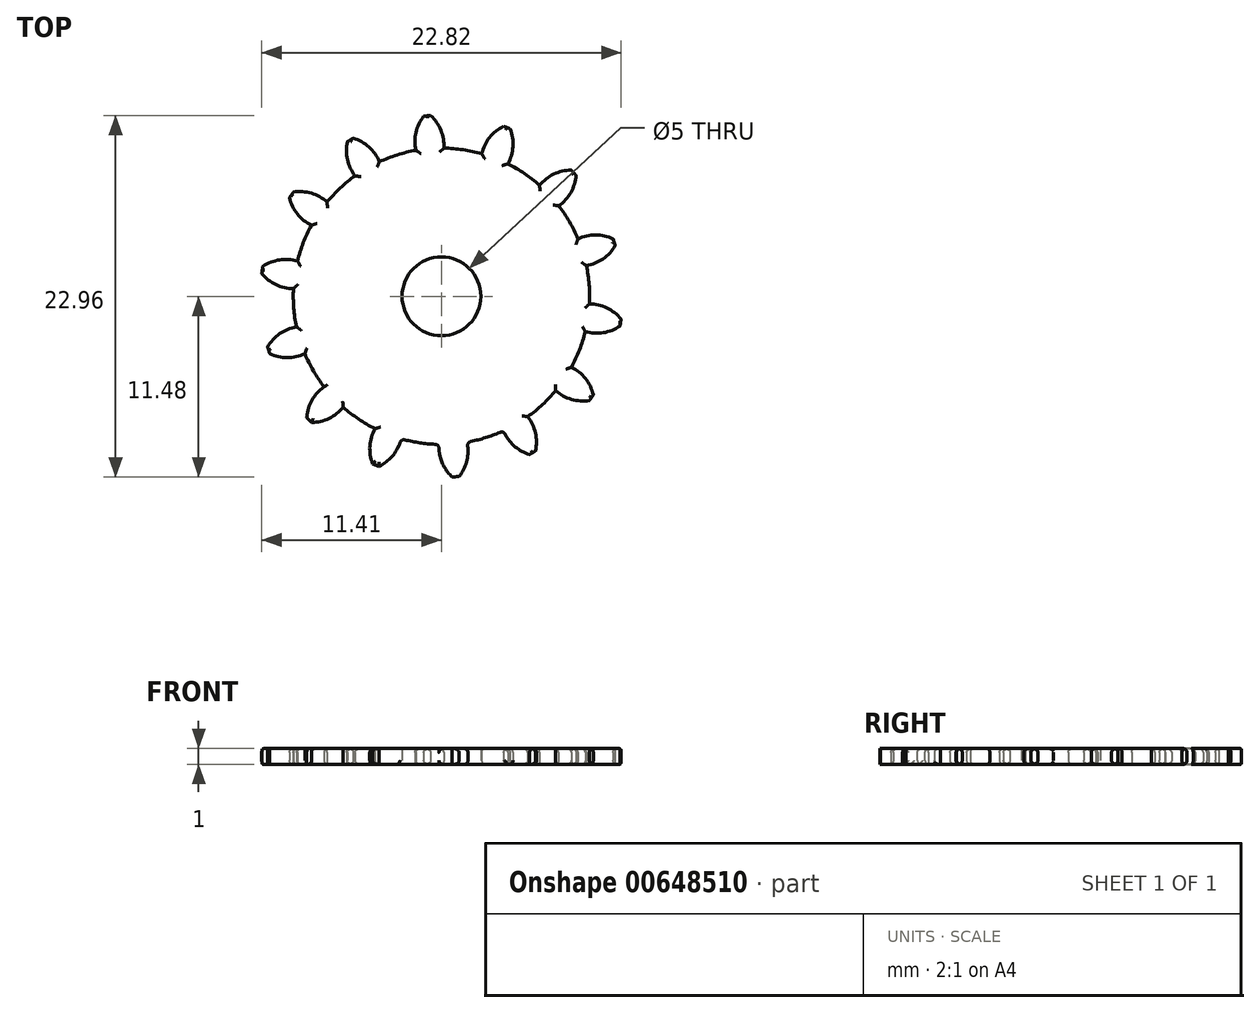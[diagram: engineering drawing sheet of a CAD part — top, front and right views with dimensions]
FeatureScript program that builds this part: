
annotation { "Feature Type Name" : "Feature", "Feature Type Description" : "" }
export const myFeature = defineFeature(function(context is Context, id is Id, definition is map)
    precondition{}
    {
        {
            assignVariable(context, id + "F0", {"name" : "GearDepth", "anyValue" : 1});
        }
        {
            assignVariable(context, id + "F1", {"name" : "TeethFillet", "anyValue" : getVariable(context, 'GearDepth') * .25});
        }
        {
            var Q0;
            Q0=qCreatedBy(makeId("Top.planeOp"),FACE);
            var sketch = newSketch(context, id + "F2", { "sketchPlane" : qUnion([Q0])});
            skCircle(sketch, "E0", {"center": v(0, 0) * mm, "radius": 9.4 * mm});
            skCircle(sketch, "E1", {"center": v(0, 0) * mm, "radius": 10.45 * mm, "construction": true});
            skCircle(sketch, "E2", {"center": v(0, 0) * mm, "radius": 11.5 * mm, "construction": true});
            skLineSegment(sketch, "E3", {"start": v(0, 0) * mm, "end": v(0, 17.6) * mm, "construction": true});
            skLineSegment(sketch, "E4", {"start": v(0, 0) * mm, "end": v(-1.42, 18) * mm, "construction": true});
            skLineSegment(sketch, "E5", {"start": v(0, 10.45) * mm, "end": v(-10.54, 10.45) * mm, "construction": true});
            skLineSegment(sketch, "E6", {"start": v(0, 10.45) * mm, "end": v(-10.3, 6.7) * mm, "construction": true});
            skCircle(sketch, "E7", {"center": v(0, 10.45) * mm, "radius": 2.61 * mm, "construction": true});
            skCircle(sketch, "E8", {"center": v(-2.46, 9.56) * mm, "radius": 2.61 * mm, "construction": true});
            skArc(sketch, "E9", {"start": v(-4.91, 10.45) * mm, "mid": v(-4.92, 10.42) * mm, "end": v(-4.94, 10.39) * mm});
            skArc(sketch, "E10.trimOffspring", {"start": v(0.15, 9.4) * mm, "mid": v(-0.03, 10.54) * mm, "end": v(-0.68, 11.48) * mm});
            skArc(sketch, "E11.MirrorCS", {"start": v(-1.62, 9.27) * mm, "mid": v(-1.62, 10.41) * mm, "end": v(-1.12, 11.45) * mm});
            skLineSegment(sketch, "E12", {"start": v(-1.12, 11.45) * mm, "end": v(-0.68, 11.48) * mm});
            skArc(sketch, "E13.1.0", {"start": v(-3.94, 8.54) * mm, "mid": v(-4.6, 9.48) * mm, "end": v(-5.6, 10.05) * mm});
            skLineSegment(sketch, "E13.1.1", {"start": v(-5.98, 9.82) * mm, "end": v(-5.6, 10.05) * mm});
            skArc(sketch, "E13.1.2", {"start": v(-5.48, 7.65) * mm, "mid": v(-5.97, 8.68) * mm, "end": v(-5.98, 9.82) * mm});
            skArc(sketch, "E13.2.0", {"start": v(-7.26, 5.99) * mm, "mid": v(-8.26, 6.55) * mm, "end": v(-9.4, 6.62) * mm});
            skLineSegment(sketch, "E13.2.1", {"start": v(-9.65, 6.26) * mm, "end": v(-9.4, 6.62) * mm});
            skArc(sketch, "E13.2.2", {"start": v(-8.26, 4.5) * mm, "mid": v(-9.15, 5.23) * mm, "end": v(-9.65, 6.26) * mm});
            skArc(sketch, "E13.3.0", {"start": v(-9.14, 2.24) * mm, "mid": v(-10.28, 2.31) * mm, "end": v(-11.34, 1.89) * mm});
            skLineSegment(sketch, "E13.3.1", {"start": v(-11.4, 1.45) * mm, "end": v(-11.34, 1.89) * mm});
            skArc(sketch, "E13.3.2", {"start": v(-9.4, 0.48) * mm, "mid": v(-10.51, 0.74) * mm, "end": v(-11.4, 1.45) * mm});
            skArc(sketch, "E13.4.0", {"start": v(-9.2, -1.94) * mm, "mid": v(-10.27, -2.38) * mm, "end": v(-11.04, -3.22) * mm});
            skLineSegment(sketch, "E13.4.1", {"start": v(-10.9, -3.64) * mm, "end": v(-11.04, -3.22) * mm});
            skArc(sketch, "E13.4.2", {"start": v(-8.67, -3.64) * mm, "mid": v(-9.8, -3.9) * mm, "end": v(-10.9, -3.64) * mm});
            skArc(sketch, "E13.5.0", {"start": v(-7.45, -5.75) * mm, "mid": v(-8.22, -6.6) * mm, "end": v(-8.55, -7.7) * mm});
            skLineSegment(sketch, "E13.5.1", {"start": v(-8.25, -8.01) * mm, "end": v(-8.55, -7.7) * mm});
            skArc(sketch, "E13.5.2", {"start": v(-6.23, -7.05) * mm, "mid": v(-7.13, -7.76) * mm, "end": v(-8.25, -8.01) * mm});
            skArc(sketch, "E13.6.0", {"start": v(-4.22, -8.4) * mm, "mid": v(-4.54, -9.5) * mm, "end": v(-4.37, -10.64) * mm});
            skLineSegment(sketch, "E13.6.1", {"start": v(-3.95, -10.8) * mm, "end": v(-4.37, -10.64) * mm});
            skArc(sketch, "E13.6.2", {"start": v(-2.56, -9.05) * mm, "mid": v(-3.06, -10.08) * mm, "end": v(-3.95, -10.8) * mm});
            skArc(sketch, "E13.7.0", {"start": v(-0.15, -9.4) * mm, "mid": v(0.03, -10.54) * mm, "end": v(0.68, -11.48) * mm});
            skLineSegment(sketch, "E13.7.1", {"start": v(1.12, -11.45) * mm, "end": v(0.68, -11.48) * mm});
            skArc(sketch, "E13.7.2", {"start": v(1.62, -9.27) * mm, "mid": v(1.62, -10.41) * mm, "end": v(1.12, -11.45) * mm});
            skArc(sketch, "E13.8.0", {"start": v(3.94, -8.54) * mm, "mid": v(4.6, -9.48) * mm, "end": v(5.6, -10.05) * mm});
            skLineSegment(sketch, "E13.8.1", {"start": v(5.98, -9.82) * mm, "end": v(5.6, -10.05) * mm});
            skArc(sketch, "E13.8.2", {"start": v(5.48, -7.65) * mm, "mid": v(5.97, -8.68) * mm, "end": v(5.98, -9.82) * mm});
            skArc(sketch, "E13.9.0", {"start": v(7.26, -5.99) * mm, "mid": v(8.26, -6.55) * mm, "end": v(9.4, -6.62) * mm});
            skLineSegment(sketch, "E13.9.1", {"start": v(9.65, -6.26) * mm, "end": v(9.4, -6.62) * mm});
            skArc(sketch, "E13.9.2", {"start": v(8.26, -4.5) * mm, "mid": v(9.15, -5.23) * mm, "end": v(9.65, -6.26) * mm});
            skArc(sketch, "E13.10.0", {"start": v(9.14, -2.24) * mm, "mid": v(10.28, -2.31) * mm, "end": v(11.34, -1.89) * mm});
            skLineSegment(sketch, "E13.10.1", {"start": v(11.4, -1.45) * mm, "end": v(11.34, -1.89) * mm});
            skArc(sketch, "E13.10.2", {"start": v(9.4, -0.48) * mm, "mid": v(10.51, -0.74) * mm, "end": v(11.4, -1.45) * mm});
            skArc(sketch, "E13.11.0", {"start": v(9.2, 1.94) * mm, "mid": v(10.27, 2.38) * mm, "end": v(11.04, 3.22) * mm});
            skLineSegment(sketch, "E13.11.1", {"start": v(10.9, 3.64) * mm, "end": v(11.04, 3.22) * mm});
            skArc(sketch, "E13.11.2", {"start": v(8.67, 3.64) * mm, "mid": v(9.8, 3.9) * mm, "end": v(10.9, 3.64) * mm});
            skArc(sketch, "E13.12.0", {"start": v(7.45, 5.75) * mm, "mid": v(8.22, 6.6) * mm, "end": v(8.55, 7.7) * mm});
            skLineSegment(sketch, "E13.12.1", {"start": v(8.25, 8.01) * mm, "end": v(8.55, 7.7) * mm});
            skArc(sketch, "E13.12.2", {"start": v(6.23, 7.05) * mm, "mid": v(7.13, 7.76) * mm, "end": v(8.25, 8.01) * mm});
            skArc(sketch, "E13.13.0", {"start": v(4.22, 8.4) * mm, "mid": v(4.54, 9.5) * mm, "end": v(4.37, 10.64) * mm});
            skLineSegment(sketch, "E13.13.1", {"start": v(3.95, 10.8) * mm, "end": v(4.37, 10.64) * mm});
            skArc(sketch, "E13.13.2", {"start": v(2.56, 9.05) * mm, "mid": v(3.06, 10.08) * mm, "end": v(3.95, 10.8) * mm});
            skCircle(sketch, "E14", {"center": v(0, 0) * mm, "radius": 2.5 * mm});
            skSolve(sketch);
        }
        {
            var Q0;
            {var subQ0=sQuery(id+"F2.wireOp",EDGE,"E10.trimOffspring");Q0=makeQuery(id+"F2.imprint","IMPRINT",FACE,{"disambiguationData":[TD([[makeQuery(id+"F2.imprint","IMPRINT",EDGE,{"derivedFrom":subQ0}),1.0]])]});}
            var Q1;
            {var subQ0=sQuery(id+"F2.wireOp",EDGE,"E0");var subQ1=makeQuery(id+"F2.imprint","INTERSECT",VERTEX,{"derivedFrom":[subQ0,sQuery(id+"F2.wireOp",EDGE,"E10.trimOffspring")]});Q1=makeQuery(id+"F2.imprint","IMPRINT",FACE,{"disambiguationData":[TD([[makeQuery(id+"F2.imprint","IMPRINT",EDGE,{"disambiguationData":[TD([[subQ1,-1.0]])],"derivedFrom":subQ0}),1.0]])]});}
            var Q2;
            {var subQ0=sQuery(id+"F2.wireOp",EDGE,"E13.1.0");Q2=makeQuery(id+"F2.imprint","IMPRINT",FACE,{"disambiguationData":[TD([[makeQuery(id+"F2.imprint","IMPRINT",EDGE,{"derivedFrom":subQ0}),1.0]])]});}
            var Q3;
            {var subQ0=sQuery(id+"F2.wireOp",EDGE,"E13.2.0");Q3=makeQuery(id+"F2.imprint","IMPRINT",FACE,{"disambiguationData":[TD([[makeQuery(id+"F2.imprint","IMPRINT",EDGE,{"derivedFrom":subQ0}),1.0]])]});}
            var Q4;
            {var subQ0=sQuery(id+"F2.wireOp",EDGE,"E13.3.0");Q4=makeQuery(id+"F2.imprint","IMPRINT",FACE,{"disambiguationData":[TD([[makeQuery(id+"F2.imprint","IMPRINT",EDGE,{"derivedFrom":subQ0}),1.0]])]});}
            var Q5;
            {var subQ0=sQuery(id+"F2.wireOp",EDGE,"E13.4.0");Q5=makeQuery(id+"F2.imprint","IMPRINT",FACE,{"disambiguationData":[TD([[makeQuery(id+"F2.imprint","IMPRINT",EDGE,{"derivedFrom":subQ0}),1.0]])]});}
            var Q6;
            {var subQ0=sQuery(id+"F2.wireOp",EDGE,"E13.5.0");Q6=makeQuery(id+"F2.imprint","IMPRINT",FACE,{"disambiguationData":[TD([[makeQuery(id+"F2.imprint","IMPRINT",EDGE,{"derivedFrom":subQ0}),1.0]])]});}
            var Q7;
            {var subQ0=sQuery(id+"F2.wireOp",EDGE,"E13.6.0");Q7=makeQuery(id+"F2.imprint","IMPRINT",FACE,{"disambiguationData":[TD([[makeQuery(id+"F2.imprint","IMPRINT",EDGE,{"derivedFrom":subQ0}),1.0]])]});}
            var Q8;
            {var subQ0=sQuery(id+"F2.wireOp",EDGE,"E13.7.0");Q8=makeQuery(id+"F2.imprint","IMPRINT",FACE,{"disambiguationData":[TD([[makeQuery(id+"F2.imprint","IMPRINT",EDGE,{"derivedFrom":subQ0}),1.0]])]});}
            var Q9;
            {var subQ0=sQuery(id+"F2.wireOp",EDGE,"E13.8.0");Q9=makeQuery(id+"F2.imprint","IMPRINT",FACE,{"disambiguationData":[TD([[makeQuery(id+"F2.imprint","IMPRINT",EDGE,{"derivedFrom":subQ0}),1.0]])]});}
            var Q10;
            {var subQ0=sQuery(id+"F2.wireOp",EDGE,"E13.9.0");Q10=makeQuery(id+"F2.imprint","IMPRINT",FACE,{"disambiguationData":[TD([[makeQuery(id+"F2.imprint","IMPRINT",EDGE,{"derivedFrom":subQ0}),1.0]])]});}
            var Q11;
            {var subQ0=sQuery(id+"F2.wireOp",EDGE,"E13.10.0");Q11=makeQuery(id+"F2.imprint","IMPRINT",FACE,{"disambiguationData":[TD([[makeQuery(id+"F2.imprint","IMPRINT",EDGE,{"derivedFrom":subQ0}),1.0]])]});}
            var Q12;
            {var subQ0=sQuery(id+"F2.wireOp",EDGE,"E13.11.0");Q12=makeQuery(id+"F2.imprint","IMPRINT",FACE,{"disambiguationData":[TD([[makeQuery(id+"F2.imprint","IMPRINT",EDGE,{"derivedFrom":subQ0}),1.0]])]});}
            var Q13;
            {var subQ0=sQuery(id+"F2.wireOp",EDGE,"E13.12.0");Q13=makeQuery(id+"F2.imprint","IMPRINT",FACE,{"disambiguationData":[TD([[makeQuery(id+"F2.imprint","IMPRINT",EDGE,{"derivedFrom":subQ0}),1.0]])]});}
            var Q14;
            {var subQ0=sQuery(id+"F2.wireOp",EDGE,"E13.13.0");Q14=makeQuery(id+"F2.imprint","IMPRINT",FACE,{"disambiguationData":[TD([[makeQuery(id+"F2.imprint","IMPRINT",EDGE,{"derivedFrom":subQ0}),1.0]])]});}
            var Q15;
            {var subQ0=sQuery(id+"F2.wireOp",EDGE,"E13.14.0");Q15=makeQuery(id+"F2.imprint","IMPRINT",FACE,{"disambiguationData":[TD([[makeQuery(id+"F2.imprint","IMPRINT",EDGE,{"derivedFrom":subQ0}),1.0]])]});}
            var Q16;
            {var subQ0=sQuery(id+"F2.wireOp",EDGE,"E13.15.0");Q16=makeQuery(id+"F2.imprint","IMPRINT",FACE,{"disambiguationData":[TD([[makeQuery(id+"F2.imprint","IMPRINT",EDGE,{"derivedFrom":subQ0}),1.0]])]});}
            var Q17;
            {var subQ0=sQuery(id+"F2.wireOp",EDGE,"E13.16.0");Q17=makeQuery(id+"F2.imprint","IMPRINT",FACE,{"disambiguationData":[TD([[makeQuery(id+"F2.imprint","IMPRINT",EDGE,{"derivedFrom":subQ0}),1.0]])]});}
            var Q18;
            {var subQ0=sQuery(id+"F2.wireOp",EDGE,"E13.17.0");Q18=makeQuery(id+"F2.imprint","IMPRINT",FACE,{"disambiguationData":[TD([[makeQuery(id+"F2.imprint","IMPRINT",EDGE,{"derivedFrom":subQ0}),1.0]])]});}
            var Q19;
            {var subQ0=sQuery(id+"F2.wireOp",EDGE,"E13.18.0");Q19=makeQuery(id+"F2.imprint","IMPRINT",FACE,{"disambiguationData":[TD([[makeQuery(id+"F2.imprint","IMPRINT",EDGE,{"derivedFrom":subQ0}),1.0]])]});}
            var Q20;
            {var subQ0=sQuery(id+"F2.wireOp",EDGE,"E13.19.0");Q20=makeQuery(id+"F2.imprint","IMPRINT",FACE,{"disambiguationData":[TD([[makeQuery(id+"F2.imprint","IMPRINT",EDGE,{"derivedFrom":subQ0}),1.0]])]});}
            var Q21;
            Q21=sQuery(id+"F2.wireOp",EDGE,"E0");
            var Q22;
            Q22=sQuery(id+"F2.wireOp",EDGE,"E10.trimOffspring");
            var Q23;
            Q23=sQuery(id+"F2.wireOp",EDGE,"E12");
            var Q24;
            Q24=sQuery(id+"F2.wireOp",EDGE,"E11.MirrorCS");
            extrude(context, id + "F3", {"entities" : qUnion([Q0, Q1, Q2, Q3, Q4, Q5, Q6, Q7, Q8, Q9, Q10, Q11, Q12, Q13, Q14, Q15, Q16, Q17, Q18, Q19, Q20]), "surfaceEntities" : qUnion([Q21, Q22, Q23, Q24]), "depth" : (getVariable(context, 'GearDepth')) * mm});
        }
        {
            var Q0;
            Q0=makeQuery(id+"F3.opExtrude","CAP_EDGE",EDGE,{"disambiguationData":[OSD([sQuery(id+"F2.wireOp",EDGE,"E13.5.2")])],"isStart":false});
            var Q1;
            Q1=makeQuery(id+"F3.opExtrude","CAP_EDGE",EDGE,{"disambiguationData":[OSD([sQuery(id+"F2.wireOp",EDGE,"E13.5.1")])],"isStart":false});
            var Q2;
            {var subQ0=sQuery(id+"F2.wireOp",EDGE,"E0");Q2=makeQuery(id+"F3.opExtrude","CAP_EDGE",EDGE,{"disambiguationData":[OSD([subQ0]),TDD([makeQuery(id+"F2.imprint","IMPRINT",EDGE,{"disambiguationData":[TD([[makeQuery(id+"F2.imprint","INTERSECT",VERTEX,{"derivedFrom":[subQ0,sQuery(id+"F2.wireOp",EDGE,"E13.5.2")]}),-1.0]])],"derivedFrom":subQ0})])],"isStart":false});}
            var Q3;
            Q3=makeQuery(id+"F3.opExtrude","CAP_EDGE",EDGE,{"disambiguationData":[OSD([sQuery(id+"F2.wireOp",EDGE,"E13.6.0")])],"isStart":false});
            var Q4;
            Q4=makeQuery(id+"F3.opExtrude","CAP_EDGE",EDGE,{"disambiguationData":[OSD([sQuery(id+"F2.wireOp",EDGE,"E13.6.1")])],"isStart":false});
            var Q5;
            Q5=makeQuery(id+"F3.opExtrude","CAP_EDGE",EDGE,{"disambiguationData":[OSD([sQuery(id+"F2.wireOp",EDGE,"E13.6.2")])],"isStart":false});
            var Q6;
            {var subQ0=sQuery(id+"F2.wireOp",EDGE,"E0");Q6=makeQuery(id+"F3.opExtrude","SWEPT_FACE",FACE,{"disambiguationData":[OSD([subQ0]),TDD([makeQuery(id+"F2.imprint","IMPRINT",EDGE,{"disambiguationData":[TD([[makeQuery(id+"F2.imprint","INTERSECT",VERTEX,{"derivedFrom":[subQ0,sQuery(id+"F2.wireOp",EDGE,"E13.6.2")]}),-1.0]])],"derivedFrom":subQ0})])]});}
            var Q7;
            {var subQ0=sQuery(id+"F2.wireOp",EDGE,"E0");Q7=makeQuery(id+"F3.opExtrude","CAP_EDGE",EDGE,{"disambiguationData":[OSD([subQ0]),TDD([makeQuery(id+"F2.imprint","IMPRINT",EDGE,{"disambiguationData":[TD([[makeQuery(id+"F2.imprint","INTERSECT",VERTEX,{"derivedFrom":[subQ0,sQuery(id+"F2.wireOp",EDGE,"E13.6.2")]}),-1.0]])],"derivedFrom":subQ0})])],"isStart":false});}
            var Q8;
            Q8=makeQuery(id+"F3.opExtrude","CAP_EDGE",EDGE,{"disambiguationData":[OSD([sQuery(id+"F2.wireOp",EDGE,"E13.7.2")])],"isStart":true});
            var Q9;
            {var subQ0=sQuery(id+"F2.wireOp",EDGE,"E0");Q9=makeQuery(id+"F3.opExtrude","CAP_EDGE",EDGE,{"disambiguationData":[OSD([subQ0]),TDD([makeQuery(id+"F2.imprint","IMPRINT",EDGE,{"disambiguationData":[TD([[makeQuery(id+"F2.imprint","INTERSECT",VERTEX,{"derivedFrom":[subQ0,sQuery(id+"F2.wireOp",EDGE,"E13.7.2")]}),-1.0]])],"derivedFrom":subQ0})])],"isStart":true});}
            var Q10;
            Q10=makeQuery(id+"F3.opExtrude","CAP_EDGE",EDGE,{"disambiguationData":[OSD([sQuery(id+"F2.wireOp",EDGE,"E13.7.2")])],"isStart":false});
            var Q11;
            {var subQ0=sQuery(id+"F2.wireOp",EDGE,"E0");Q11=makeQuery(id+"F3.opExtrude","CAP_EDGE",EDGE,{"disambiguationData":[OSD([subQ0]),TDD([makeQuery(id+"F2.imprint","IMPRINT",EDGE,{"disambiguationData":[TD([[makeQuery(id+"F2.imprint","INTERSECT",VERTEX,{"derivedFrom":[subQ0,sQuery(id+"F2.wireOp",EDGE,"E13.7.2")]}),-1.0]])],"derivedFrom":subQ0})])],"isStart":false});}
            var Q12;
            Q12=makeQuery(id+"F3.opExtrude","CAP_EDGE",EDGE,{"disambiguationData":[OSD([sQuery(id+"F2.wireOp",EDGE,"E13.8.0")])],"isStart":false});
            var Q13;
            {var subQ0=sQuery(id+"F2.wireOp",EDGE,"E0");Q13=makeQuery(id+"F3.opExtrude","SWEPT_FACE",FACE,{"disambiguationData":[OSD([subQ0]),TDD([makeQuery(id+"F2.imprint","IMPRINT",EDGE,{"disambiguationData":[TD([[makeQuery(id+"F2.imprint","INTERSECT",VERTEX,{"derivedFrom":[subQ0,sQuery(id+"F2.wireOp",EDGE,"E13.7.2")]}),-1.0]])],"derivedFrom":subQ0})])]});}
            var Q14;
            Q14=makeQuery(id+"F3.opExtrude","CAP_EDGE",EDGE,{"disambiguationData":[OSD([sQuery(id+"F2.wireOp",EDGE,"E13.6.0")])],"isStart":true});
            var Q15;
            Q15=makeQuery(id+"F3.opExtrude","CAP_EDGE",EDGE,{"disambiguationData":[OSD([sQuery(id+"F2.wireOp",EDGE,"E13.8.2")])],"isStart":false});
            var Q16;
            {var subQ0=sQuery(id+"F2.wireOp",EDGE,"E0");Q16=makeQuery(id+"F3.opExtrude","CAP_EDGE",EDGE,{"disambiguationData":[OSD([subQ0]),TDD([makeQuery(id+"F2.imprint","IMPRINT",EDGE,{"disambiguationData":[TD([[makeQuery(id+"F2.imprint","INTERSECT",VERTEX,{"derivedFrom":[subQ0,sQuery(id+"F2.wireOp",EDGE,"E13.8.2")]}),-1.0]])],"derivedFrom":subQ0})])],"isStart":false});}
            var Q17;
            Q17=makeQuery(id+"F3.opExtrude","CAP_EDGE",EDGE,{"disambiguationData":[OSD([sQuery(id+"F2.wireOp",EDGE,"E13.9.0")])],"isStart":false});
            var Q18;
            Q18=makeQuery(id+"F3.opExtrude","CAP_EDGE",EDGE,{"disambiguationData":[OSD([sQuery(id+"F2.wireOp",EDGE,"E13.9.2")])],"isStart":false});
            var Q19;
            {var subQ0=sQuery(id+"F2.wireOp",EDGE,"E0");Q19=makeQuery(id+"F3.opExtrude","CAP_EDGE",EDGE,{"disambiguationData":[OSD([subQ0]),TDD([makeQuery(id+"F2.imprint","IMPRINT",EDGE,{"disambiguationData":[TD([[makeQuery(id+"F2.imprint","INTERSECT",VERTEX,{"derivedFrom":[subQ0,sQuery(id+"F2.wireOp",EDGE,"E13.9.2")]}),-1.0]])],"derivedFrom":subQ0})])],"isStart":false});}
            var Q20;
            Q20=makeQuery(id+"F3.opExtrude","CAP_EDGE",EDGE,{"disambiguationData":[OSD([sQuery(id+"F2.wireOp",EDGE,"E13.10.0")])],"isStart":false});
            var Q21;
            Q21=makeQuery(id+"F3.opExtrude","CAP_EDGE",EDGE,{"disambiguationData":[OSD([sQuery(id+"F2.wireOp",EDGE,"E13.10.2")])],"isStart":false});
            var Q22;
            {var subQ0=sQuery(id+"F2.wireOp",EDGE,"E0");Q22=makeQuery(id+"F3.opExtrude","CAP_EDGE",EDGE,{"disambiguationData":[OSD([subQ0]),TDD([makeQuery(id+"F2.imprint","IMPRINT",EDGE,{"disambiguationData":[TD([[makeQuery(id+"F2.imprint","INTERSECT",VERTEX,{"derivedFrom":[subQ0,sQuery(id+"F2.wireOp",EDGE,"E13.10.2")]}),-1.0]])],"derivedFrom":subQ0})])],"isStart":false});}
            var Q23;
            Q23=makeQuery(id+"F3.opExtrude","CAP_EDGE",EDGE,{"disambiguationData":[OSD([sQuery(id+"F2.wireOp",EDGE,"E13.11.0")])],"isStart":false});
            var Q24;
            Q24=makeQuery(id+"F3.opExtrude","CAP_EDGE",EDGE,{"disambiguationData":[OSD([sQuery(id+"F2.wireOp",EDGE,"E13.11.2")])],"isStart":false});
            var Q25;
            {var subQ0=sQuery(id+"F2.wireOp",EDGE,"E0");Q25=makeQuery(id+"F3.opExtrude","CAP_EDGE",EDGE,{"disambiguationData":[OSD([subQ0]),TDD([makeQuery(id+"F2.imprint","IMPRINT",EDGE,{"disambiguationData":[TD([[makeQuery(id+"F2.imprint","INTERSECT",VERTEX,{"derivedFrom":[subQ0,sQuery(id+"F2.wireOp",EDGE,"E13.11.2")]}),-1.0]])],"derivedFrom":subQ0})])],"isStart":false});}
            var Q26;
            Q26=makeQuery(id+"F3.opExtrude","CAP_EDGE",EDGE,{"disambiguationData":[OSD([sQuery(id+"F2.wireOp",EDGE,"E13.12.0")])],"isStart":false});
            var Q27;
            Q27=makeQuery(id+"F3.opExtrude","CAP_EDGE",EDGE,{"disambiguationData":[OSD([sQuery(id+"F2.wireOp",EDGE,"E13.12.2")])],"isStart":false});
            var Q28;
            {var subQ0=sQuery(id+"F2.wireOp",EDGE,"E0");Q28=makeQuery(id+"F3.opExtrude","CAP_EDGE",EDGE,{"disambiguationData":[OSD([subQ0]),TDD([makeQuery(id+"F2.imprint","IMPRINT",EDGE,{"disambiguationData":[TD([[makeQuery(id+"F2.imprint","INTERSECT",VERTEX,{"derivedFrom":[subQ0,sQuery(id+"F2.wireOp",EDGE,"E13.12.2")]}),-1.0]])],"derivedFrom":subQ0})])],"isStart":false});}
            var Q29;
            Q29=makeQuery(id+"F3.opExtrude","CAP_EDGE",EDGE,{"disambiguationData":[OSD([sQuery(id+"F2.wireOp",EDGE,"E13.13.0")])],"isStart":false});
            var Q30;
            Q30=makeQuery(id+"F3.opExtrude","CAP_EDGE",EDGE,{"disambiguationData":[OSD([sQuery(id+"F2.wireOp",EDGE,"E13.13.2")])],"isStart":false});
            var Q31;
            {var subQ0=sQuery(id+"F2.wireOp",EDGE,"E0");Q31=makeQuery(id+"F3.opExtrude","CAP_EDGE",EDGE,{"disambiguationData":[OSD([subQ0]),TDD([makeQuery(id+"F2.imprint","IMPRINT",EDGE,{"disambiguationData":[TD([[makeQuery(id+"F2.imprint","INTERSECT",VERTEX,{"derivedFrom":[subQ0,sQuery(id+"F2.wireOp",EDGE,"E13.13.2")]}),-1.0]])],"derivedFrom":subQ0})])],"isStart":false});}
            var Q32;
            Q32=makeQuery(id+"F3.opExtrude","CAP_EDGE",EDGE,{"disambiguationData":[OSD([sQuery(id+"F2.wireOp",EDGE,"E13.14.0")])],"isStart":false});
            var Q33;
            Q33=makeQuery(id+"F3.opExtrude","CAP_EDGE",EDGE,{"disambiguationData":[OSD([sQuery(id+"F2.wireOp",EDGE,"E13.14.2")])],"isStart":false});
            var Q34;
            {var subQ0=sQuery(id+"F2.wireOp",EDGE,"E0");Q34=makeQuery(id+"F3.opExtrude","CAP_EDGE",EDGE,{"disambiguationData":[OSD([subQ0]),TDD([makeQuery(id+"F2.imprint","IMPRINT",EDGE,{"disambiguationData":[TD([[makeQuery(id+"F2.imprint","INTERSECT",VERTEX,{"derivedFrom":[subQ0,sQuery(id+"F2.wireOp",EDGE,"E13.14.2")]}),-1.0]])],"derivedFrom":subQ0})])],"isStart":false});}
            var Q35;
            Q35=makeQuery(id+"F3.opExtrude","CAP_EDGE",EDGE,{"disambiguationData":[OSD([sQuery(id+"F2.wireOp",EDGE,"E13.15.0")])],"isStart":false});
            var Q36;
            {var subQ0=sQuery(id+"F2.wireOp",EDGE,"E0");Q36=makeQuery(id+"F3.opExtrude","CAP_EDGE",EDGE,{"disambiguationData":[OSD([subQ0]),TDD([makeQuery(id+"F2.imprint","IMPRINT",EDGE,{"disambiguationData":[TD([[makeQuery(id+"F2.imprint","INTERSECT",VERTEX,{"derivedFrom":[subQ0,sQuery(id+"F2.wireOp",EDGE,"E13.14.2")]}),-1.0]])],"derivedFrom":subQ0})])],"isStart":false});}
            var Q37;
            Q37=makeQuery(id+"F3.opExtrude","CAP_EDGE",EDGE,{"disambiguationData":[OSD([sQuery(id+"F2.wireOp",EDGE,"E13.15.2")])],"isStart":false});
            var Q38;
            {var subQ0=sQuery(id+"F2.wireOp",EDGE,"E0");Q38=makeQuery(id+"F3.opExtrude","CAP_EDGE",EDGE,{"disambiguationData":[OSD([subQ0]),TDD([makeQuery(id+"F2.imprint","IMPRINT",EDGE,{"disambiguationData":[TD([[makeQuery(id+"F2.imprint","INTERSECT",VERTEX,{"derivedFrom":[subQ0,sQuery(id+"F2.wireOp",EDGE,"E13.15.2")]}),-1.0]])],"derivedFrom":subQ0})])],"isStart":false});}
            var Q39;
            Q39=makeQuery(id+"F3.opExtrude","CAP_EDGE",EDGE,{"disambiguationData":[OSD([sQuery(id+"F2.wireOp",EDGE,"E13.16.0")])],"isStart":false});
            var Q40;
            Q40=makeQuery(id+"F3.opExtrude","CAP_EDGE",EDGE,{"disambiguationData":[OSD([sQuery(id+"F2.wireOp",EDGE,"E13.16.2")])],"isStart":false});
            var Q41;
            Q41=makeQuery(id+"F3.opExtrude","CAP_EDGE",EDGE,{"disambiguationData":[OSD([sQuery(id+"F2.wireOp",EDGE,"E13.17.0")])],"isStart":false});
            var Q42;
            {var subQ0=sQuery(id+"F2.wireOp",EDGE,"E0");Q42=makeQuery(id+"F3.opExtrude","CAP_EDGE",EDGE,{"disambiguationData":[OSD([subQ0]),TDD([makeQuery(id+"F2.imprint","IMPRINT",EDGE,{"disambiguationData":[TD([[makeQuery(id+"F2.imprint","INTERSECT",VERTEX,{"derivedFrom":[subQ0,sQuery(id+"F2.wireOp",EDGE,"E13.16.2")]}),-1.0]])],"derivedFrom":subQ0})])],"isStart":false});}
            var Q43;
            Q43=makeQuery(id+"F3.opExtrude","CAP_EDGE",EDGE,{"disambiguationData":[OSD([sQuery(id+"F2.wireOp",EDGE,"E13.17.2")])],"isStart":false});
            var Q44;
            {var subQ0=sQuery(id+"F2.wireOp",EDGE,"E0");Q44=makeQuery(id+"F3.opExtrude","CAP_EDGE",EDGE,{"disambiguationData":[OSD([subQ0]),TDD([makeQuery(id+"F2.imprint","IMPRINT",EDGE,{"disambiguationData":[TD([[makeQuery(id+"F2.imprint","INTERSECT",VERTEX,{"derivedFrom":[subQ0,sQuery(id+"F2.wireOp",EDGE,"E13.17.2")]}),-1.0]])],"derivedFrom":subQ0})])],"isStart":false});}
            var Q45;
            Q45=makeQuery(id+"F3.opExtrude","CAP_EDGE",EDGE,{"disambiguationData":[OSD([sQuery(id+"F2.wireOp",EDGE,"E13.18.0")])],"isStart":false});
            var Q46;
            Q46=makeQuery(id+"F3.opExtrude","CAP_EDGE",EDGE,{"disambiguationData":[OSD([sQuery(id+"F2.wireOp",EDGE,"E13.18.2")])],"isStart":false});
            var Q47;
            {var subQ0=sQuery(id+"F2.wireOp",EDGE,"E0");Q47=makeQuery(id+"F3.opExtrude","CAP_EDGE",EDGE,{"disambiguationData":[OSD([subQ0]),TDD([makeQuery(id+"F2.imprint","IMPRINT",EDGE,{"disambiguationData":[TD([[makeQuery(id+"F2.imprint","INTERSECT",VERTEX,{"derivedFrom":[subQ0,sQuery(id+"F2.wireOp",EDGE,"E13.18.2")]}),-1.0]])],"derivedFrom":subQ0})])],"isStart":false});}
            var Q48;
            Q48=makeQuery(id+"F3.opExtrude","CAP_EDGE",EDGE,{"disambiguationData":[OSD([sQuery(id+"F2.wireOp",EDGE,"E13.19.0")])],"isStart":false});
            var Q49;
            Q49=makeQuery(id+"F3.opExtrude","CAP_EDGE",EDGE,{"disambiguationData":[OSD([sQuery(id+"F2.wireOp",EDGE,"E13.19.2")])],"isStart":false});
            var Q50;
            Q50=makeQuery(id+"F3.opExtrude","CAP_EDGE",EDGE,{"disambiguationData":[OSD([sQuery(id+"F2.wireOp",EDGE,"E10.trimOffspring")])],"isStart":false});
            var Q51;
            Q51=makeQuery(id+"F3.opExtrude","CAP_EDGE",EDGE,{"disambiguationData":[OSD([sQuery(id+"F2.wireOp",EDGE,"E11.MirrorCS")])],"isStart":false});
            var Q52;
            {var subQ0=sQuery(id+"F2.wireOp",EDGE,"E0");Q52=makeQuery(id+"F3.opExtrude","CAP_EDGE",EDGE,{"disambiguationData":[OSD([subQ0]),TDD([makeQuery(id+"F2.imprint","IMPRINT",EDGE,{"disambiguationData":[TD([[makeQuery(id+"F2.imprint","INTERSECT",VERTEX,{"derivedFrom":[subQ0,sQuery(id+"F2.wireOp",EDGE,"E11.MirrorCS")]}),-1.0]])],"derivedFrom":subQ0})])],"isStart":false});}
            var Q53;
            Q53=makeQuery(id+"F3.opExtrude","CAP_EDGE",EDGE,{"disambiguationData":[OSD([sQuery(id+"F2.wireOp",EDGE,"E13.1.0")])],"isStart":false});
            var Q54;
            Q54=makeQuery(id+"F3.opExtrude","CAP_EDGE",EDGE,{"disambiguationData":[OSD([sQuery(id+"F2.wireOp",EDGE,"E13.1.2")])],"isStart":false});
            var Q55;
            {var subQ0=sQuery(id+"F2.wireOp",EDGE,"E0");Q55=makeQuery(id+"F3.opExtrude","CAP_EDGE",EDGE,{"disambiguationData":[OSD([subQ0]),TDD([makeQuery(id+"F2.imprint","IMPRINT",EDGE,{"disambiguationData":[TD([[makeQuery(id+"F2.imprint","INTERSECT",VERTEX,{"derivedFrom":[subQ0,sQuery(id+"F2.wireOp",EDGE,"E13.1.2")]}),-1.0]])],"derivedFrom":subQ0})])],"isStart":false});}
            var Q56;
            Q56=makeQuery(id+"F3.opExtrude","CAP_EDGE",EDGE,{"disambiguationData":[OSD([sQuery(id+"F2.wireOp",EDGE,"E13.2.0")])],"isStart":false});
            var Q57;
            Q57=makeQuery(id+"F3.opExtrude","CAP_EDGE",EDGE,{"disambiguationData":[OSD([sQuery(id+"F2.wireOp",EDGE,"E13.2.2")])],"isStart":false});
            var Q58;
            {var subQ0=sQuery(id+"F2.wireOp",EDGE,"E0");Q58=makeQuery(id+"F3.opExtrude","CAP_EDGE",EDGE,{"disambiguationData":[OSD([subQ0]),TDD([makeQuery(id+"F2.imprint","IMPRINT",EDGE,{"disambiguationData":[TD([[makeQuery(id+"F2.imprint","INTERSECT",VERTEX,{"derivedFrom":[subQ0,sQuery(id+"F2.wireOp",EDGE,"E13.2.2")]}),-1.0]])],"derivedFrom":subQ0})])],"isStart":false});}
            var Q59;
            Q59=makeQuery(id+"F3.opExtrude","CAP_EDGE",EDGE,{"disambiguationData":[OSD([sQuery(id+"F2.wireOp",EDGE,"E13.3.0")])],"isStart":false});
            var Q60;
            Q60=makeQuery(id+"F3.opExtrude","CAP_EDGE",EDGE,{"disambiguationData":[OSD([sQuery(id+"F2.wireOp",EDGE,"E13.3.2")])],"isStart":false});
            var Q61;
            {var subQ0=sQuery(id+"F2.wireOp",EDGE,"E0");Q61=makeQuery(id+"F3.opExtrude","CAP_EDGE",EDGE,{"disambiguationData":[OSD([subQ0]),TDD([makeQuery(id+"F2.imprint","IMPRINT",EDGE,{"disambiguationData":[TD([[makeQuery(id+"F2.imprint","INTERSECT",VERTEX,{"derivedFrom":[subQ0,sQuery(id+"F2.wireOp",EDGE,"E13.3.2")]}),-1.0]])],"derivedFrom":subQ0})])],"isStart":false});}
            var Q62;
            Q62=makeQuery(id+"F3.opExtrude","CAP_EDGE",EDGE,{"disambiguationData":[OSD([sQuery(id+"F2.wireOp",EDGE,"E13.4.0")])],"isStart":false});
            var Q63;
            Q63=makeQuery(id+"F3.opExtrude","CAP_EDGE",EDGE,{"disambiguationData":[OSD([sQuery(id+"F2.wireOp",EDGE,"E13.4.2")])],"isStart":false});
            var Q64;
            {var subQ0=sQuery(id+"F2.wireOp",EDGE,"E0");Q64=makeQuery(id+"F3.opExtrude","CAP_EDGE",EDGE,{"disambiguationData":[OSD([subQ0]),TDD([makeQuery(id+"F2.imprint","IMPRINT",EDGE,{"disambiguationData":[TD([[makeQuery(id+"F2.imprint","INTERSECT",VERTEX,{"derivedFrom":[subQ0,sQuery(id+"F2.wireOp",EDGE,"E13.4.2")]}),-1.0]])],"derivedFrom":subQ0})])],"isStart":false});}
            var Q65;
            {var subQ0=sQuery(id+"F2.wireOp",EDGE,"E0");Q65=makeQuery(id+"F3.opExtrude","CAP_EDGE",EDGE,{"disambiguationData":[OSD([subQ0]),TDD([makeQuery(id+"F2.imprint","IMPRINT",EDGE,{"disambiguationData":[TD([[makeQuery(id+"F2.imprint","INTERSECT",VERTEX,{"derivedFrom":[subQ0,sQuery(id+"F2.wireOp",EDGE,"E13.5.2")]}),-1.0]])],"derivedFrom":subQ0})])],"isStart":true});}
            var Q66;
            Q66=makeQuery(id+"F3.opExtrude","CAP_EDGE",EDGE,{"disambiguationData":[OSD([sQuery(id+"F2.wireOp",EDGE,"E13.5.2")])],"isStart":true});
            var Q67;
            {var subQ0=sQuery(id+"F2.wireOp",EDGE,"E0");Q67=makeQuery(id+"F3.opExtrude","CAP_EDGE",EDGE,{"disambiguationData":[OSD([subQ0]),TDD([makeQuery(id+"F2.imprint","IMPRINT",EDGE,{"disambiguationData":[TD([[makeQuery(id+"F2.imprint","INTERSECT",VERTEX,{"derivedFrom":[subQ0,sQuery(id+"F2.wireOp",EDGE,"E13.4.2")]}),-1.0]])],"derivedFrom":subQ0})])],"isStart":true});}
            var Q68;
            Q68=makeQuery(id+"F3.opExtrude","CAP_EDGE",EDGE,{"disambiguationData":[OSD([sQuery(id+"F2.wireOp",EDGE,"E13.4.2")])],"isStart":true});
            var Q69;
            Q69=makeQuery(id+"F3.opExtrude","CAP_EDGE",EDGE,{"disambiguationData":[OSD([sQuery(id+"F2.wireOp",EDGE,"E13.4.0")])],"isStart":true});
            var Q70;
            {var subQ0=sQuery(id+"F2.wireOp",EDGE,"E0");Q70=makeQuery(id+"F3.opExtrude","CAP_EDGE",EDGE,{"disambiguationData":[OSD([subQ0]),TDD([makeQuery(id+"F2.imprint","IMPRINT",EDGE,{"disambiguationData":[TD([[makeQuery(id+"F2.imprint","INTERSECT",VERTEX,{"derivedFrom":[subQ0,sQuery(id+"F2.wireOp",EDGE,"E13.3.2")]}),-1.0]])],"derivedFrom":subQ0})])],"isStart":true});}
            var Q71;
            Q71=makeQuery(id+"F3.opExtrude","CAP_EDGE",EDGE,{"disambiguationData":[OSD([sQuery(id+"F2.wireOp",EDGE,"E13.3.2")])],"isStart":true});
            var Q72;
            Q72=makeQuery(id+"F3.opExtrude","CAP_EDGE",EDGE,{"disambiguationData":[OSD([sQuery(id+"F2.wireOp",EDGE,"E13.3.0")])],"isStart":true});
            var Q73;
            {var subQ0=sQuery(id+"F2.wireOp",EDGE,"E0");Q73=makeQuery(id+"F3.opExtrude","CAP_EDGE",EDGE,{"disambiguationData":[OSD([subQ0]),TDD([makeQuery(id+"F2.imprint","IMPRINT",EDGE,{"disambiguationData":[TD([[makeQuery(id+"F2.imprint","INTERSECT",VERTEX,{"derivedFrom":[subQ0,sQuery(id+"F2.wireOp",EDGE,"E13.2.2")]}),-1.0]])],"derivedFrom":subQ0})])],"isStart":true});}
            var Q74;
            Q74=makeQuery(id+"F3.opExtrude","CAP_EDGE",EDGE,{"disambiguationData":[OSD([sQuery(id+"F2.wireOp",EDGE,"E13.2.2")])],"isStart":true});
            var Q75;
            Q75=makeQuery(id+"F3.opExtrude","CAP_EDGE",EDGE,{"disambiguationData":[OSD([sQuery(id+"F2.wireOp",EDGE,"E13.2.0")])],"isStart":true});
            var Q76;
            Q76=makeQuery(id+"F3.opExtrude","CAP_EDGE",EDGE,{"disambiguationData":[OSD([sQuery(id+"F2.wireOp",EDGE,"E13.1.2")])],"isStart":true});
            var Q77;
            {var subQ0=sQuery(id+"F2.wireOp",EDGE,"E0");Q77=makeQuery(id+"F3.opExtrude","CAP_EDGE",EDGE,{"disambiguationData":[OSD([subQ0]),TDD([makeQuery(id+"F2.imprint","IMPRINT",EDGE,{"disambiguationData":[TD([[makeQuery(id+"F2.imprint","INTERSECT",VERTEX,{"derivedFrom":[subQ0,sQuery(id+"F2.wireOp",EDGE,"E13.1.2")]}),-1.0]])],"derivedFrom":subQ0})])],"isStart":true});}
            var Q78;
            Q78=makeQuery(id+"F3.opExtrude","CAP_EDGE",EDGE,{"disambiguationData":[OSD([sQuery(id+"F2.wireOp",EDGE,"E13.1.0")])],"isStart":true});
            var Q79;
            {var subQ0=sQuery(id+"F2.wireOp",EDGE,"E0");Q79=makeQuery(id+"F3.opExtrude","CAP_EDGE",EDGE,{"disambiguationData":[OSD([subQ0]),TDD([makeQuery(id+"F2.imprint","IMPRINT",EDGE,{"disambiguationData":[TD([[makeQuery(id+"F2.imprint","INTERSECT",VERTEX,{"derivedFrom":[subQ0,sQuery(id+"F2.wireOp",EDGE,"E11.MirrorCS")]}),-1.0]])],"derivedFrom":subQ0})])],"isStart":true});}
            var Q80;
            Q80=makeQuery(id+"F3.opExtrude","CAP_EDGE",EDGE,{"disambiguationData":[OSD([sQuery(id+"F2.wireOp",EDGE,"E11.MirrorCS")])],"isStart":true});
            var Q81;
            Q81=makeQuery(id+"F3.opExtrude","CAP_EDGE",EDGE,{"disambiguationData":[OSD([sQuery(id+"F2.wireOp",EDGE,"E10.trimOffspring")])],"isStart":true});
            var Q82;
            {var subQ0=sQuery(id+"F2.wireOp",EDGE,"E0");Q82=makeQuery(id+"F3.opExtrude","CAP_EDGE",EDGE,{"disambiguationData":[OSD([subQ0]),TDD([makeQuery(id+"F2.imprint","IMPRINT",EDGE,{"disambiguationData":[TD([[makeQuery(id+"F2.imprint","INTERSECT",VERTEX,{"derivedFrom":[subQ0,sQuery(id+"F2.wireOp",EDGE,"E10.trimOffspring")]}),1.0]])],"derivedFrom":subQ0})])],"isStart":true});}
            var Q83;
            Q83=makeQuery(id+"F3.opExtrude","CAP_EDGE",EDGE,{"disambiguationData":[OSD([sQuery(id+"F2.wireOp",EDGE,"E13.19.2")])],"isStart":true});
            var Q84;
            Q84=makeQuery(id+"F3.opExtrude","CAP_EDGE",EDGE,{"disambiguationData":[OSD([sQuery(id+"F2.wireOp",EDGE,"E13.19.0")])],"isStart":true});
            var Q85;
            {var subQ0=sQuery(id+"F2.wireOp",EDGE,"E0");Q85=makeQuery(id+"F3.opExtrude","CAP_EDGE",EDGE,{"disambiguationData":[OSD([subQ0]),TDD([makeQuery(id+"F2.imprint","IMPRINT",EDGE,{"disambiguationData":[TD([[makeQuery(id+"F2.imprint","INTERSECT",VERTEX,{"derivedFrom":[subQ0,sQuery(id+"F2.wireOp",EDGE,"E13.18.2")]}),-1.0]])],"derivedFrom":subQ0})])],"isStart":true});}
            var Q86;
            Q86=makeQuery(id+"F3.opExtrude","CAP_EDGE",EDGE,{"disambiguationData":[OSD([sQuery(id+"F2.wireOp",EDGE,"E13.18.2")])],"isStart":true});
            var Q87;
            Q87=makeQuery(id+"F3.opExtrude","CAP_EDGE",EDGE,{"disambiguationData":[OSD([sQuery(id+"F2.wireOp",EDGE,"E13.18.0")])],"isStart":true});
            var Q88;
            {var subQ0=sQuery(id+"F2.wireOp",EDGE,"E0");Q88=makeQuery(id+"F3.opExtrude","CAP_EDGE",EDGE,{"disambiguationData":[OSD([subQ0]),TDD([makeQuery(id+"F2.imprint","IMPRINT",EDGE,{"disambiguationData":[TD([[makeQuery(id+"F2.imprint","INTERSECT",VERTEX,{"derivedFrom":[subQ0,sQuery(id+"F2.wireOp",EDGE,"E13.17.2")]}),-1.0]])],"derivedFrom":subQ0})])],"isStart":true});}
            var Q89;
            Q89=makeQuery(id+"F3.opExtrude","CAP_EDGE",EDGE,{"disambiguationData":[OSD([sQuery(id+"F2.wireOp",EDGE,"E13.17.2")])],"isStart":true});
            var Q90;
            Q90=makeQuery(id+"F3.opExtrude","CAP_EDGE",EDGE,{"disambiguationData":[OSD([sQuery(id+"F2.wireOp",EDGE,"E13.17.0")])],"isStart":true});
            var Q91;
            {var subQ0=sQuery(id+"F2.wireOp",EDGE,"E0");Q91=makeQuery(id+"F3.opExtrude","CAP_EDGE",EDGE,{"disambiguationData":[OSD([subQ0]),TDD([makeQuery(id+"F2.imprint","IMPRINT",EDGE,{"disambiguationData":[TD([[makeQuery(id+"F2.imprint","INTERSECT",VERTEX,{"derivedFrom":[subQ0,sQuery(id+"F2.wireOp",EDGE,"E13.16.2")]}),-1.0]])],"derivedFrom":subQ0})])],"isStart":true});}
            var Q92;
            Q92=makeQuery(id+"F3.opExtrude","CAP_EDGE",EDGE,{"disambiguationData":[OSD([sQuery(id+"F2.wireOp",EDGE,"E13.16.2")])],"isStart":true});
            var Q93;
            Q93=makeQuery(id+"F3.opExtrude","CAP_EDGE",EDGE,{"disambiguationData":[OSD([sQuery(id+"F2.wireOp",EDGE,"E13.16.0")])],"isStart":true});
            var Q94;
            {var subQ0=sQuery(id+"F2.wireOp",EDGE,"E0");Q94=makeQuery(id+"F3.opExtrude","CAP_EDGE",EDGE,{"disambiguationData":[OSD([subQ0]),TDD([makeQuery(id+"F2.imprint","IMPRINT",EDGE,{"disambiguationData":[TD([[makeQuery(id+"F2.imprint","INTERSECT",VERTEX,{"derivedFrom":[subQ0,sQuery(id+"F2.wireOp",EDGE,"E13.15.2")]}),-1.0]])],"derivedFrom":subQ0})])],"isStart":true});}
            var Q95;
            Q95=makeQuery(id+"F3.opExtrude","CAP_EDGE",EDGE,{"disambiguationData":[OSD([sQuery(id+"F2.wireOp",EDGE,"E13.15.2")])],"isStart":true});
            var Q96;
            Q96=makeQuery(id+"F3.opExtrude","CAP_EDGE",EDGE,{"disambiguationData":[OSD([sQuery(id+"F2.wireOp",EDGE,"E13.15.0")])],"isStart":true});
            var Q97;
            {var subQ0=sQuery(id+"F2.wireOp",EDGE,"E0");Q97=makeQuery(id+"F3.opExtrude","CAP_EDGE",EDGE,{"disambiguationData":[OSD([subQ0]),TDD([makeQuery(id+"F2.imprint","IMPRINT",EDGE,{"disambiguationData":[TD([[makeQuery(id+"F2.imprint","INTERSECT",VERTEX,{"derivedFrom":[subQ0,sQuery(id+"F2.wireOp",EDGE,"E13.14.2")]}),-1.0]])],"derivedFrom":subQ0})])],"isStart":true});}
            var Q98;
            Q98=makeQuery(id+"F3.opExtrude","CAP_EDGE",EDGE,{"disambiguationData":[OSD([sQuery(id+"F2.wireOp",EDGE,"E13.14.2")])],"isStart":true});
            var Q99;
            Q99=makeQuery(id+"F3.opExtrude","CAP_EDGE",EDGE,{"disambiguationData":[OSD([sQuery(id+"F2.wireOp",EDGE,"E13.14.0")])],"isStart":true});
            var Q100;
            {var subQ0=sQuery(id+"F2.wireOp",EDGE,"E0");Q100=makeQuery(id+"F3.opExtrude","CAP_EDGE",EDGE,{"disambiguationData":[OSD([subQ0]),TDD([makeQuery(id+"F2.imprint","IMPRINT",EDGE,{"disambiguationData":[TD([[makeQuery(id+"F2.imprint","INTERSECT",VERTEX,{"derivedFrom":[subQ0,sQuery(id+"F2.wireOp",EDGE,"E13.13.2")]}),-1.0]])],"derivedFrom":subQ0})])],"isStart":true});}
            var Q101;
            Q101=makeQuery(id+"F3.opExtrude","CAP_EDGE",EDGE,{"disambiguationData":[OSD([sQuery(id+"F2.wireOp",EDGE,"E13.13.2")])],"isStart":true});
            var Q102;
            Q102=makeQuery(id+"F3.opExtrude","CAP_EDGE",EDGE,{"disambiguationData":[OSD([sQuery(id+"F2.wireOp",EDGE,"E13.13.0")])],"isStart":true});
            var Q103;
            {var subQ0=sQuery(id+"F2.wireOp",EDGE,"E0");Q103=makeQuery(id+"F3.opExtrude","CAP_EDGE",EDGE,{"disambiguationData":[OSD([subQ0]),TDD([makeQuery(id+"F2.imprint","IMPRINT",EDGE,{"disambiguationData":[TD([[makeQuery(id+"F2.imprint","INTERSECT",VERTEX,{"derivedFrom":[subQ0,sQuery(id+"F2.wireOp",EDGE,"E13.12.2")]}),-1.0]])],"derivedFrom":subQ0})])],"isStart":true});}
            var Q104;
            Q104=makeQuery(id+"F3.opExtrude","CAP_EDGE",EDGE,{"disambiguationData":[OSD([sQuery(id+"F2.wireOp",EDGE,"E13.12.2")])],"isStart":true});
            var Q105;
            Q105=makeQuery(id+"F3.opExtrude","CAP_EDGE",EDGE,{"disambiguationData":[OSD([sQuery(id+"F2.wireOp",EDGE,"E13.12.0")])],"isStart":true});
            var Q106;
            {var subQ0=sQuery(id+"F2.wireOp",EDGE,"E0");Q106=makeQuery(id+"F3.opExtrude","CAP_EDGE",EDGE,{"disambiguationData":[OSD([subQ0]),TDD([makeQuery(id+"F2.imprint","IMPRINT",EDGE,{"disambiguationData":[TD([[makeQuery(id+"F2.imprint","INTERSECT",VERTEX,{"derivedFrom":[subQ0,sQuery(id+"F2.wireOp",EDGE,"E13.11.2")]}),-1.0]])],"derivedFrom":subQ0})])],"isStart":true});}
            var Q107;
            Q107=makeQuery(id+"F3.opExtrude","CAP_EDGE",EDGE,{"disambiguationData":[OSD([sQuery(id+"F2.wireOp",EDGE,"E13.11.2")])],"isStart":true});
            var Q108;
            Q108=makeQuery(id+"F3.opExtrude","CAP_EDGE",EDGE,{"disambiguationData":[OSD([sQuery(id+"F2.wireOp",EDGE,"E13.11.0")])],"isStart":true});
            var Q109;
            {var subQ0=sQuery(id+"F2.wireOp",EDGE,"E0");Q109=makeQuery(id+"F3.opExtrude","CAP_EDGE",EDGE,{"disambiguationData":[OSD([subQ0]),TDD([makeQuery(id+"F2.imprint","IMPRINT",EDGE,{"disambiguationData":[TD([[makeQuery(id+"F2.imprint","INTERSECT",VERTEX,{"derivedFrom":[subQ0,sQuery(id+"F2.wireOp",EDGE,"E13.10.2")]}),-1.0]])],"derivedFrom":subQ0})])],"isStart":true});}
            var Q110;
            Q110=makeQuery(id+"F3.opExtrude","CAP_EDGE",EDGE,{"disambiguationData":[OSD([sQuery(id+"F2.wireOp",EDGE,"E13.10.2")])],"isStart":true});
            var Q111;
            Q111=makeQuery(id+"F3.opExtrude","CAP_EDGE",EDGE,{"disambiguationData":[OSD([sQuery(id+"F2.wireOp",EDGE,"E13.10.0")])],"isStart":true});
            var Q112;
            {var subQ0=sQuery(id+"F2.wireOp",EDGE,"E0");Q112=makeQuery(id+"F3.opExtrude","CAP_EDGE",EDGE,{"disambiguationData":[OSD([subQ0]),TDD([makeQuery(id+"F2.imprint","IMPRINT",EDGE,{"disambiguationData":[TD([[makeQuery(id+"F2.imprint","INTERSECT",VERTEX,{"derivedFrom":[subQ0,sQuery(id+"F2.wireOp",EDGE,"E13.9.2")]}),-1.0]])],"derivedFrom":subQ0})])],"isStart":true});}
            var Q113;
            Q113=makeQuery(id+"F3.opExtrude","CAP_EDGE",EDGE,{"disambiguationData":[OSD([sQuery(id+"F2.wireOp",EDGE,"E13.9.2")])],"isStart":true});
            var Q114;
            Q114=makeQuery(id+"F3.opExtrude","CAP_EDGE",EDGE,{"disambiguationData":[OSD([sQuery(id+"F2.wireOp",EDGE,"E13.9.0")])],"isStart":true});
            var Q115;
            {var subQ0=sQuery(id+"F2.wireOp",EDGE,"E0");Q115=makeQuery(id+"F3.opExtrude","CAP_EDGE",EDGE,{"disambiguationData":[OSD([subQ0]),TDD([makeQuery(id+"F2.imprint","IMPRINT",EDGE,{"disambiguationData":[TD([[makeQuery(id+"F2.imprint","INTERSECT",VERTEX,{"derivedFrom":[subQ0,sQuery(id+"F2.wireOp",EDGE,"E13.8.2")]}),-1.0]])],"derivedFrom":subQ0})])],"isStart":true});}
            var Q116;
            Q116=makeQuery(id+"F3.opExtrude","CAP_EDGE",EDGE,{"disambiguationData":[OSD([sQuery(id+"F2.wireOp",EDGE,"E13.8.2")])],"isStart":true});
            fillet(context, id + "F4", {"entities" : qUnion([Q0, Q1, Q2, Q3, Q4, Q5, Q6, Q7, Q8, Q9, Q10, Q11, Q12, Q13, Q14, Q15, Q16, Q17, Q18, Q19, Q20, Q21, Q22, Q23, Q24, Q25, Q26, Q27, Q28, Q29, Q30, Q31, Q32, Q33, Q34, Q35, Q36, Q37, Q38, Q39, Q40, Q41, Q42, Q43, Q44, Q45, Q46, Q47, Q48, Q49, Q50, Q51, Q52, Q53, Q54, Q55, Q56, Q57, Q58, Q59, Q60, Q61, Q62, Q63, Q64, Q65, Q66, Q67, Q68, Q69, Q70, Q71, Q72, Q73, Q74, Q75, Q76, Q77, Q78, Q79, Q80, Q81, Q82, Q83, Q84, Q85, Q86, Q87, Q88, Q89, Q90, Q91, Q92, Q93, Q94, Q95, Q96, Q97, Q98, Q99, Q100, Q101, Q102, Q103, Q104, Q105, Q106, Q107, Q108, Q109, Q110, Q111, Q112, Q113, Q114, Q115, Q116]), "radius" : (getVariable(context, 'TeethFillet')) * mm, "tangentPropagation" : true, "allowEdgeOverflow" : false});
        }
    });
